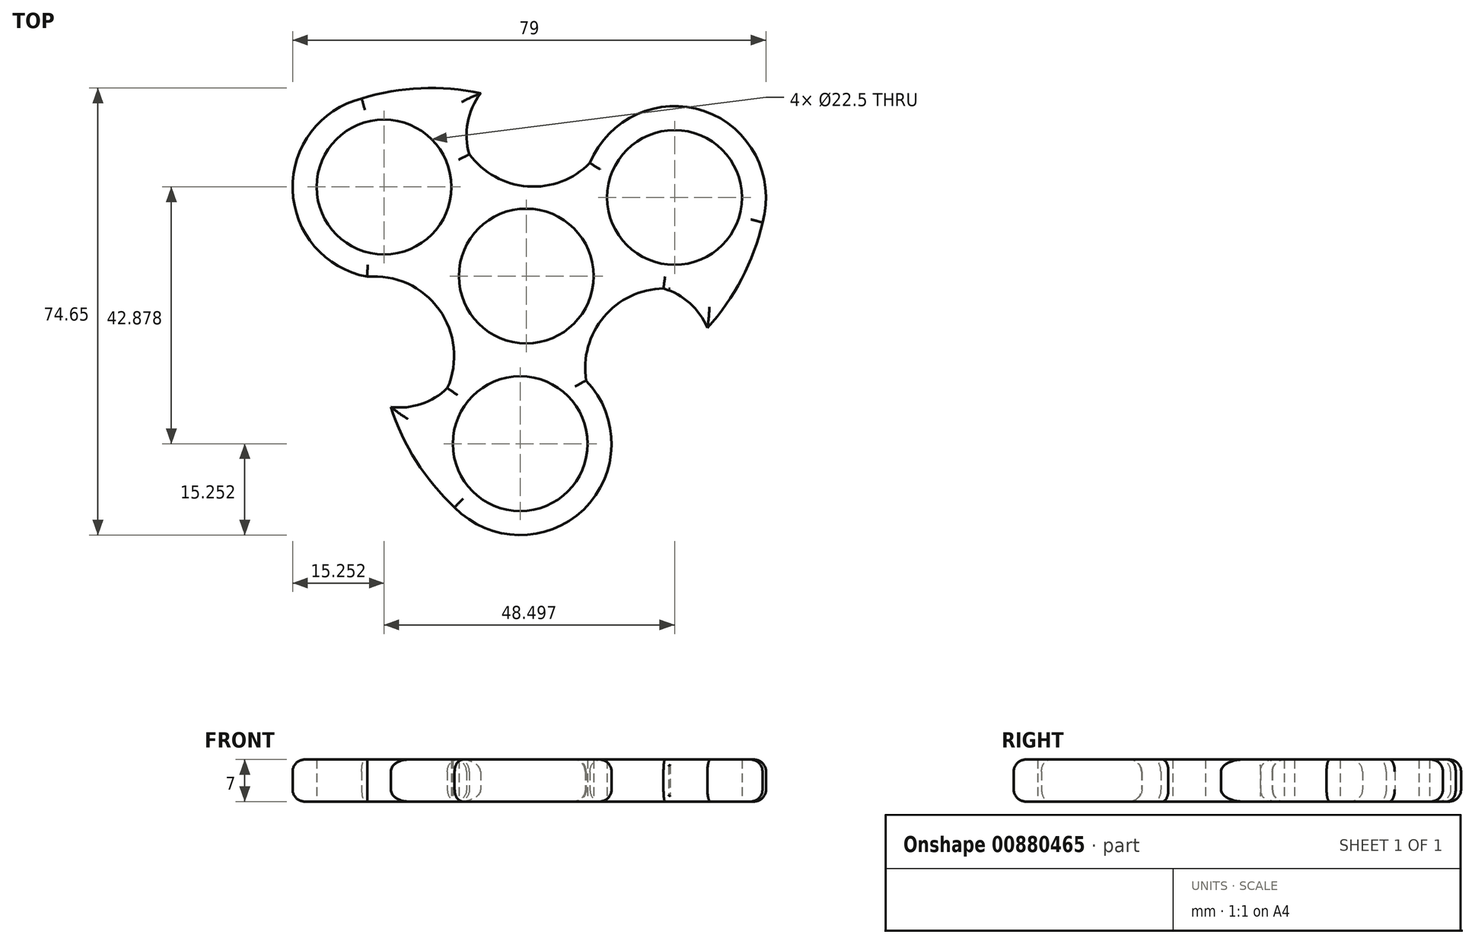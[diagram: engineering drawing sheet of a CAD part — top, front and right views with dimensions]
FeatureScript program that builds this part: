
annotation { "Feature Type Name" : "Feature", "Feature Type Description" : "" }
export const myFeature = defineFeature(function(context is Context, id is Id, definition is map)
    precondition{}
    {
        {
            var Q0;
            Q0=qCreatedBy(makeId("Top.planeOp"),FACE);
            var sketch = newSketch(context, id + "F0", { "sketchPlane" : qUnion([Q0])});
            skCircle(sketch, "E0", {"center": v(-432.99, 817.06) * mm, "radius": 11.25 * mm});
            skCircle(sketch, "E1", {"center": v(-434, 789.06) * mm, "radius": 11.25 * mm});
            skCircle(sketch, "E2.1.0", {"center": v(-408.23, 830.18) * mm, "radius": 11.25 * mm});
            skCircle(sketch, "E2.2.0", {"center": v(-456.73, 831.94) * mm, "radius": 11.25 * mm});
            skCircle(sketch, "E3.0", {"center": v(-456.73, 831.94) * mm, "radius": 15.25 * mm});
            skCircle(sketch, "E4.0", {"center": v(-408.23, 830.18) * mm, "radius": 15.25 * mm});
            skCircle(sketch, "E5.0", {"center": v(-434, 789.06) * mm, "radius": 15.25 * mm});
            skArc(sketch, "E6", {"start": v(-447.75, 795.65) * mm, "mid": v(-446.69, 810.16) * mm, "end": v(-459.54, 816.95) * mm});
            skArc(sketch, "E7", {"start": v(-442.49, 837.4) * mm, "mid": v(-432.75, 832.04) * mm, "end": v(-422.35, 835.95) * mm});
            skArc(sketch, "E8", {"start": v(-408.95, 814.95) * mm, "mid": v(-419.67, 810.66) * mm, "end": v(-422.99, 799.61) * mm});
            skArc(sketch, "E9", {"start": v(-440.62, 847.56) * mm, "mid": v(-450.59, 848.43) * mm, "end": v(-460.45, 846.73) * mm});
            skArc(sketch, "E10", {"start": v(-440.62, 847.56) * mm, "mid": v(-442.77, 842.7) * mm, "end": v(-442.49, 837.4) * mm});
            skArc(sketch, "E11.1.0", {"start": v(-455.58, 795.2) * mm, "mid": v(-451.35, 786.13) * mm, "end": v(-444.94, 778.44) * mm});
            skArc(sketch, "E11.1.1", {"start": v(-455.58, 795.2) * mm, "mid": v(-450.3, 795.76) * mm, "end": v(-445.84, 798.67) * mm});
            skArc(sketch, "E11.2.0", {"start": v(-402.76, 808.42) * mm, "mid": v(-397.02, 816.62) * mm, "end": v(-393.56, 826.02) * mm});
            skArc(sketch, "E11.2.1", {"start": v(-402.76, 808.42) * mm, "mid": v(-405.88, 812.72) * mm, "end": v(-410.63, 815.12) * mm});
            skSolve(sketch);
        }
        {
            var Q0;
            {var subQ0=sQuery(id+"F0.wireOp",EDGE,"E6");var subQ1=sQuery(id+"F0.wireOp",EDGE,"E3.0");var subQ2=makeQuery(id+"F0.imprint","INTERSECT",VERTEX,{"disambiguationData":[OD(0.0)],"derivedFrom":[subQ1,subQ0]});Q0=makeQuery(id+"F0.imprint","IMPRINT",FACE,{"disambiguationData":[TD([[makeQuery(id+"F0.imprint","IMPRINT",EDGE,{"disambiguationData":[TD([[subQ2,-1.0]])],"derivedFrom":subQ1}),1.0]])]});}
            var Q1;
            {var subQ2=sQuery(id+"F0.wireOp",EDGE,"E9");Q1=makeQuery(id+"F0.imprint","IMPRINT",FACE,{"disambiguationData":[TD([[makeQuery(id+"F0.imprint","IMPRINT",EDGE,{"derivedFrom":subQ2}),1.0]])]});}
            var Q2;
            {var subQ0=sQuery(id+"F0.wireOp",EDGE,"E11.2.1");var subQ1=sQuery(id+"F0.wireOp",EDGE,"E4.0");var subQ2=makeQuery(id+"F0.imprint","INTERSECT",VERTEX,{"derivedFrom":[subQ1,subQ0]});Q2=makeQuery(id+"F0.imprint","IMPRINT",FACE,{"disambiguationData":[TD([[makeQuery(id+"F0.imprint","IMPRINT",EDGE,{"disambiguationData":[TD([[subQ2,-1.0]])],"derivedFrom":subQ1}),-1.0]])]});}
            var Q3;
            {var subQ5=sQuery(id+"F0.wireOp",EDGE,"E11.2.0");Q3=makeQuery(id+"F0.imprint","IMPRINT",FACE,{"disambiguationData":[TD([[makeQuery(id+"F0.imprint","IMPRINT",EDGE,{"derivedFrom":subQ5}),1.0]])]});}
            var Q4;
            {var subQ0=sQuery(id+"F0.wireOp",EDGE,"E11.1.1");var subQ1=sQuery(id+"F0.wireOp",EDGE,"E5.0");var subQ2=makeQuery(id+"F0.imprint","INTERSECT",VERTEX,{"derivedFrom":[subQ1,subQ0]});Q4=makeQuery(id+"F0.imprint","IMPRINT",FACE,{"disambiguationData":[TD([[makeQuery(id+"F0.imprint","IMPRINT",EDGE,{"disambiguationData":[TD([[subQ2,-1.0]])],"derivedFrom":subQ1}),-1.0]])]});}
            var Q5;
            {var subQ0=sQuery(id+"F0.wireOp",EDGE,"E11.1.0");Q5=makeQuery(id+"F0.imprint","IMPRINT",FACE,{"disambiguationData":[TD([[makeQuery(id+"F0.imprint","IMPRINT",EDGE,{"derivedFrom":subQ0}),1.0]])]});}
            var Q6;
            Q6=makeQuery(id+"F0.imprint","IMPRINT",FACE,{"disambiguationData":[TD([[makeQuery(id+"F0.imprint","IMPRINT",EDGE,{"derivedFrom":sQuery(id+"F0.wireOp",EDGE,"E1")}),-1.0]])]});
            var Q7;
            Q7=makeQuery(id+"F0.imprint","IMPRINT",FACE,{"disambiguationData":[TD([[makeQuery(id+"F0.imprint","IMPRINT",EDGE,{"derivedFrom":sQuery(id+"F0.wireOp",EDGE,"E2.1.0")}),-1.0]])]});
            var Q8;
            Q8=makeQuery(id+"F0.imprint","IMPRINT",FACE,{"disambiguationData":[TD([[makeQuery(id+"F0.imprint","IMPRINT",EDGE,{"derivedFrom":sQuery(id+"F0.wireOp",EDGE,"E0")}),-1.0]])]});
            var Q9;
            {var subQ0=sQuery(id+"F0.wireOp",EDGE,"E6");var subQ1=sQuery(id+"F0.wireOp",EDGE,"E5.0");var subQ2=makeQuery(id+"F0.imprint","INTERSECT",VERTEX,{"disambiguationData":[OD(0.0)],"derivedFrom":[subQ1,subQ0]});Q9=makeQuery(id+"F0.imprint","IMPRINT",FACE,{"disambiguationData":[TD([[makeQuery(id+"F0.imprint","IMPRINT",EDGE,{"disambiguationData":[TD([[subQ2,1.0]])],"derivedFrom":subQ1}),1.0]])]});}
            var Q10;
            Q10=makeQuery(id+"F0.imprint","IMPRINT",FACE,{"disambiguationData":[TD([[makeQuery(id+"F0.imprint","IMPRINT",EDGE,{"derivedFrom":sQuery(id+"F0.wireOp",EDGE,"E2.2.0")}),-1.0]])]});
            extrude(context, id + "F1", {"entities" : qUnion([Q0, Q1, Q2, Q3, Q4, Q5, Q6, Q7, Q8, Q9, Q10]), "depth" : 7 * mm, "offsetDistance" : 25 * mm});
        }
        {
            var Q0;
            Q0=makeQuery(id+"F1.opExtrude","CAP_EDGE",EDGE,{"disambiguationData":[OSD([sQuery(id+"F0.wireOp",EDGE,"E11.2.0")])],"isStart":false});
            var Q1;
            {var subQ0=sQuery(id+"F0.wireOp",EDGE,"E4.0");Q1=makeQuery(id+"F1.opExtrude","CAP_EDGE",EDGE,{"disambiguationData":[OSD([subQ0]),TDD([makeQuery(id+"F0.imprint","IMPRINT",EDGE,{"disambiguationData":[TD([[makeQuery(id+"F0.imprint","INTERSECT",VERTEX,{"derivedFrom":[subQ0,sQuery(id+"F0.wireOp",EDGE,"E7")]}),1.0]])],"derivedFrom":subQ0})])],"isStart":false});}
            var Q2;
            Q2=makeQuery(id+"F1.opExtrude","CAP_EDGE",EDGE,{"disambiguationData":[OSD([sQuery(id+"F0.wireOp",EDGE,"E7")])],"isStart":false});
            var Q3;
            Q3=makeQuery(id+"F1.opExtrude","CAP_EDGE",EDGE,{"disambiguationData":[OSD([sQuery(id+"F0.wireOp",EDGE,"E10")])],"isStart":false});
            var Q4;
            Q4=makeQuery(id+"F1.opExtrude","CAP_EDGE",EDGE,{"disambiguationData":[OSD([sQuery(id+"F0.wireOp",EDGE,"E9")])],"isStart":false});
            var Q5;
            Q5=makeQuery(id+"F1.opExtrude","CAP_EDGE",EDGE,{"disambiguationData":[OSD([sQuery(id+"F0.wireOp",EDGE,"E3.0")])],"isStart":false});
            var Q6;
            Q6=makeQuery(id+"F1.opExtrude","CAP_EDGE",EDGE,{"disambiguationData":[OSD([sQuery(id+"F0.wireOp",EDGE,"E6")])],"isStart":false});
            var Q7;
            Q7=makeQuery(id+"F1.opExtrude","CAP_EDGE",EDGE,{"disambiguationData":[OSD([sQuery(id+"F0.wireOp",EDGE,"E11.1.1")])],"isStart":false});
            var Q8;
            Q8=makeQuery(id+"F1.opExtrude","CAP_EDGE",EDGE,{"disambiguationData":[OSD([sQuery(id+"F0.wireOp",EDGE,"E11.1.0")])],"isStart":false});
            var Q9;
            Q9=makeQuery(id+"F1.opExtrude","CAP_EDGE",EDGE,{"disambiguationData":[OSD([sQuery(id+"F0.wireOp",EDGE,"E5.0")])],"isStart":false});
            var Q10;
            {var subQ0=sQuery(id+"F0.wireOp",EDGE,"E8");Q10=makeQuery(id+"F1.opExtrude","CAP_EDGE",EDGE,{"disambiguationData":[OSD([subQ0]),TDD([makeQuery(id+"F0.imprint","IMPRINT",EDGE,{"disambiguationData":[TD([[makeQuery(id+"F0.imprint","INTERSECT",VERTEX,{"derivedFrom":[sQuery(id+"F0.wireOp",EDGE,"E5.0"),subQ0]}),1.0]])],"derivedFrom":subQ0})])],"isStart":false});}
            var Q11;
            Q11=makeQuery(id+"F1.opExtrude","CAP_EDGE",EDGE,{"disambiguationData":[OSD([sQuery(id+"F0.wireOp",EDGE,"E11.2.1")])],"isStart":false});
            fillet(context, id + "F2", {"entities" : qUnion([Q0, Q1, Q2, Q3, Q4, Q5, Q6, Q7, Q8, Q9, Q10, Q11]), "radius" : 2 * mm, "tangentPropagation" : true, "allowEdgeOverflow" : false});
        }
        {
            var Q0;
            {var subQ0=sQuery(id+"F0.wireOp",EDGE,"E4.0");Q0=makeQuery(id+"F1.opExtrude","CAP_EDGE",EDGE,{"disambiguationData":[OSD([subQ0]),TDD([makeQuery(id+"F0.imprint","IMPRINT",EDGE,{"disambiguationData":[TD([[makeQuery(id+"F0.imprint","INTERSECT",VERTEX,{"derivedFrom":[subQ0,sQuery(id+"F0.wireOp",EDGE,"E7")]}),1.0]])],"derivedFrom":subQ0})])],"isStart":true});}
            var Q1;
            Q1=makeQuery(id+"F1.opExtrude","CAP_EDGE",EDGE,{"disambiguationData":[OSD([sQuery(id+"F0.wireOp",EDGE,"E10")])],"isStart":true});
            var Q2;
            Q2=makeQuery(id+"F1.opExtrude","CAP_EDGE",EDGE,{"disambiguationData":[OSD([sQuery(id+"F0.wireOp",EDGE,"E9")])],"isStart":true});
            var Q3;
            Q3=makeQuery(id+"F1.opExtrude","CAP_EDGE",EDGE,{"disambiguationData":[OSD([sQuery(id+"F0.wireOp",EDGE,"E3.0")])],"isStart":true});
            var Q4;
            Q4=makeQuery(id+"F1.opExtrude","CAP_EDGE",EDGE,{"disambiguationData":[OSD([sQuery(id+"F0.wireOp",EDGE,"E6")])],"isStart":true});
            var Q5;
            Q5=makeQuery(id+"F1.opExtrude","CAP_EDGE",EDGE,{"disambiguationData":[OSD([sQuery(id+"F0.wireOp",EDGE,"E11.1.1")])],"isStart":true});
            var Q6;
            Q6=makeQuery(id+"F1.opExtrude","CAP_EDGE",EDGE,{"disambiguationData":[OSD([sQuery(id+"F0.wireOp",EDGE,"E11.1.0")])],"isStart":true});
            var Q7;
            Q7=makeQuery(id+"F1.opExtrude","CAP_EDGE",EDGE,{"disambiguationData":[OSD([sQuery(id+"F0.wireOp",EDGE,"E5.0")])],"isStart":true});
            var Q8;
            {var subQ0=sQuery(id+"F0.wireOp",EDGE,"E8");Q8=makeQuery(id+"F1.opExtrude","CAP_EDGE",EDGE,{"disambiguationData":[OSD([subQ0]),TDD([makeQuery(id+"F0.imprint","IMPRINT",EDGE,{"disambiguationData":[TD([[makeQuery(id+"F0.imprint","INTERSECT",VERTEX,{"derivedFrom":[sQuery(id+"F0.wireOp",EDGE,"E5.0"),subQ0]}),1.0]])],"derivedFrom":subQ0})])],"isStart":true});}
            var Q9;
            Q9=makeQuery(id+"F1.opExtrude","CAP_EDGE",EDGE,{"disambiguationData":[OSD([sQuery(id+"F0.wireOp",EDGE,"E11.2.1")])],"isStart":true});
            var Q10;
            Q10=makeQuery(id+"F1.opExtrude","CAP_EDGE",EDGE,{"disambiguationData":[OSD([sQuery(id+"F0.wireOp",EDGE,"E7")])],"isStart":true});
            var Q11;
            Q11=makeQuery(id+"F1.opExtrude","CAP_EDGE",EDGE,{"disambiguationData":[OSD([sQuery(id+"F0.wireOp",EDGE,"E11.2.0")])],"isStart":true});
            fillet(context, id + "F3", {"entities" : qUnion([Q0, Q1, Q2, Q3, Q4, Q5, Q6, Q7, Q8, Q9, Q10, Q11]), "radius" : 2 * mm, "tangentPropagation" : true, "allowEdgeOverflow" : false});
        }
    });
